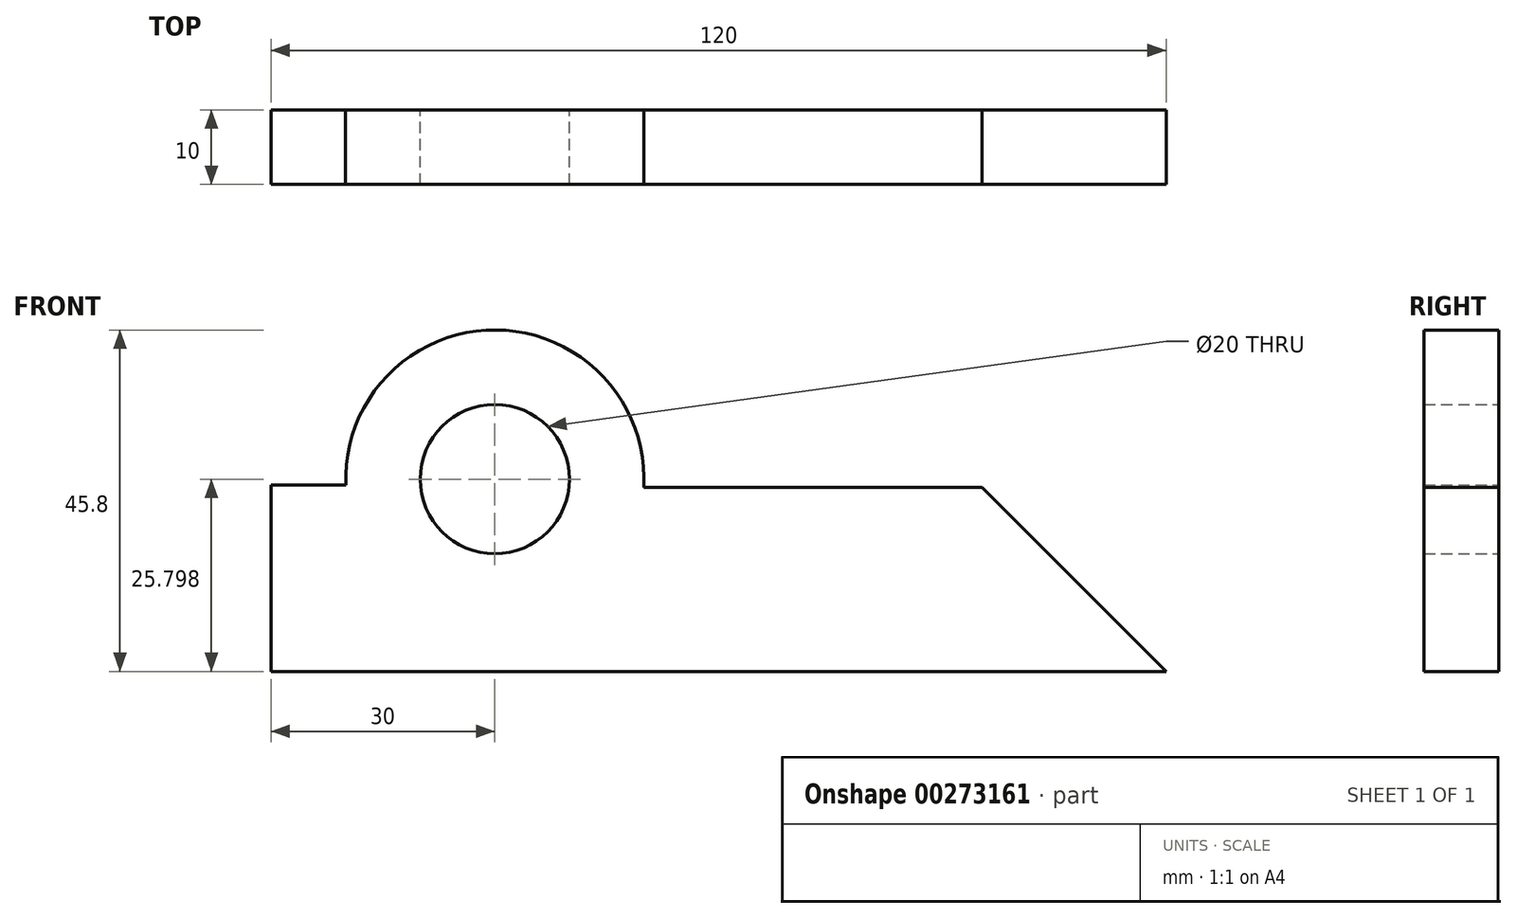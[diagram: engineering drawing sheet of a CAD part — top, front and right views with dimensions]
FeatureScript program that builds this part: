
annotation { "Feature Type Name" : "Feature", "Feature Type Description" : "" }
export const myFeature = defineFeature(function(context is Context, id is Id, definition is map)
    precondition{}
    {
        {
            var Q0;
            Q0=qCreatedBy(makeId("Front.planeOp"),FACE);
            var sketch = newSketch(context, id + "F0", { "sketchPlane" : qUnion([Q0])});
            skLineSegment(sketch, "E0", {"start": v(0, 0) * mm, "end": v(120, 0) * mm});
            skLineSegment(sketch, "E1", {"start": v(0, 0) * mm, "end": v(0, 25) * mm});
            skArc(sketch, "E2", {"start": v(49.97, 24.7) * mm, "mid": v(30.15, 45.8) * mm, "end": v(10.02, 25) * mm});
            skLineSegment(sketch, "E3", {"start": v(0, 25) * mm, "end": v(10.02, 25) * mm});
            skLineSegment(sketch, "E4", {"start": v(49.97, 24.7) * mm, "end": v(95.3, 24.7) * mm});
            skCircle(sketch, "E5", {"center": v(30, 25.8) * mm, "radius": 10 * mm});
            skLineSegment(sketch, "E6", {"start": v(120, 0) * mm, "end": v(95.3, 24.7) * mm});
            skSolve(sketch);
        }
        {
            var Q0;
            Q0 = qSketchRegion(id + "F0", true);
            extrude(context, id + "F1", {"entities" : qUnion([Q0]), "depth" : 10 * mm});
        }
    });
